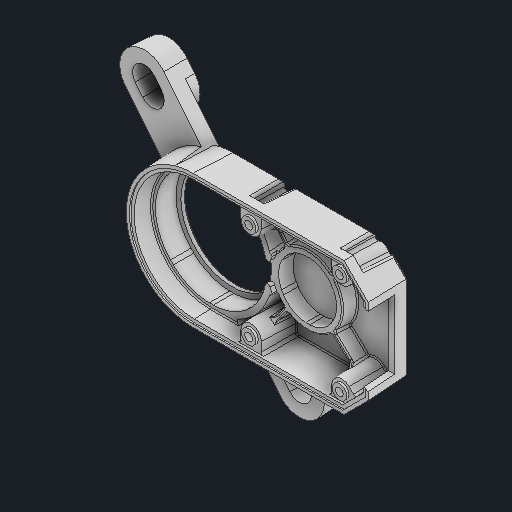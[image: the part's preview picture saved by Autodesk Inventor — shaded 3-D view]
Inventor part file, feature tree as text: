
AUTODESK INVENTOR PART (.ipt)
format: ipt  version: 2024 (Build 280153000, 153)  size: 858,112 bytes
history: native  units: in
note: dims shown in document units (in); Inventor stores cm internally (conversion verified against a paired STEP export)
features: fillet x1
ambient origin geometry x8: Origin, YZ Plane, XZ Plane, XY Plane, X Axis, Y Axis, Z Axis, Center Point
bodies: Solid1 (feature_tree)
feature tree (1):
  fillet  "Fillet11"  [1 undecoded]
note: 1 required parameter value undecoded (feature->parameter linkage not recoverable at this tier; creation-order binding heuristic only, values carry confidence <= 0.55)
